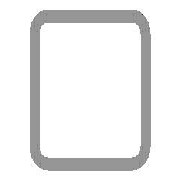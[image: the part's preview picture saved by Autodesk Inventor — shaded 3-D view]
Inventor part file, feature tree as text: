
AUTODESK INVENTOR PART (.ipt)
format: ipt  version: 2025.1 (Build 291241020, 241B)  size: 142,336 bytes
history: native  units: mm (DEFAULTED — no unit token found)
features: other x4, sketch x1, plane x1
ambient origin geometry x8: Origin, YZ Plane, XZ Plane, XY Plane, X Axis, Y Axis, Z Axis, Center Point
bodies: Solid1 (feature_tree), Body (feature_tree)
feature tree (6):
  parser-record x1  (decoder bookkeeping rows leaked as tree rows — omitted from the tree; the rows remain in map.json)
  other  "Driven Length"
  other  "Start Plane"
  other  "End Plane"
  sketch  "Sketch3"  dims[d3=950.0mm d4=0.0mm d7=8.0mm d9=100.0mm d11=100.0mm d12=4.0mm d13=50.0mm d14=1000.0mm d15=50.0mm d16=50.0mm d17=90.0deg d18=950.0mm]
  plane  "Work Plane3"
